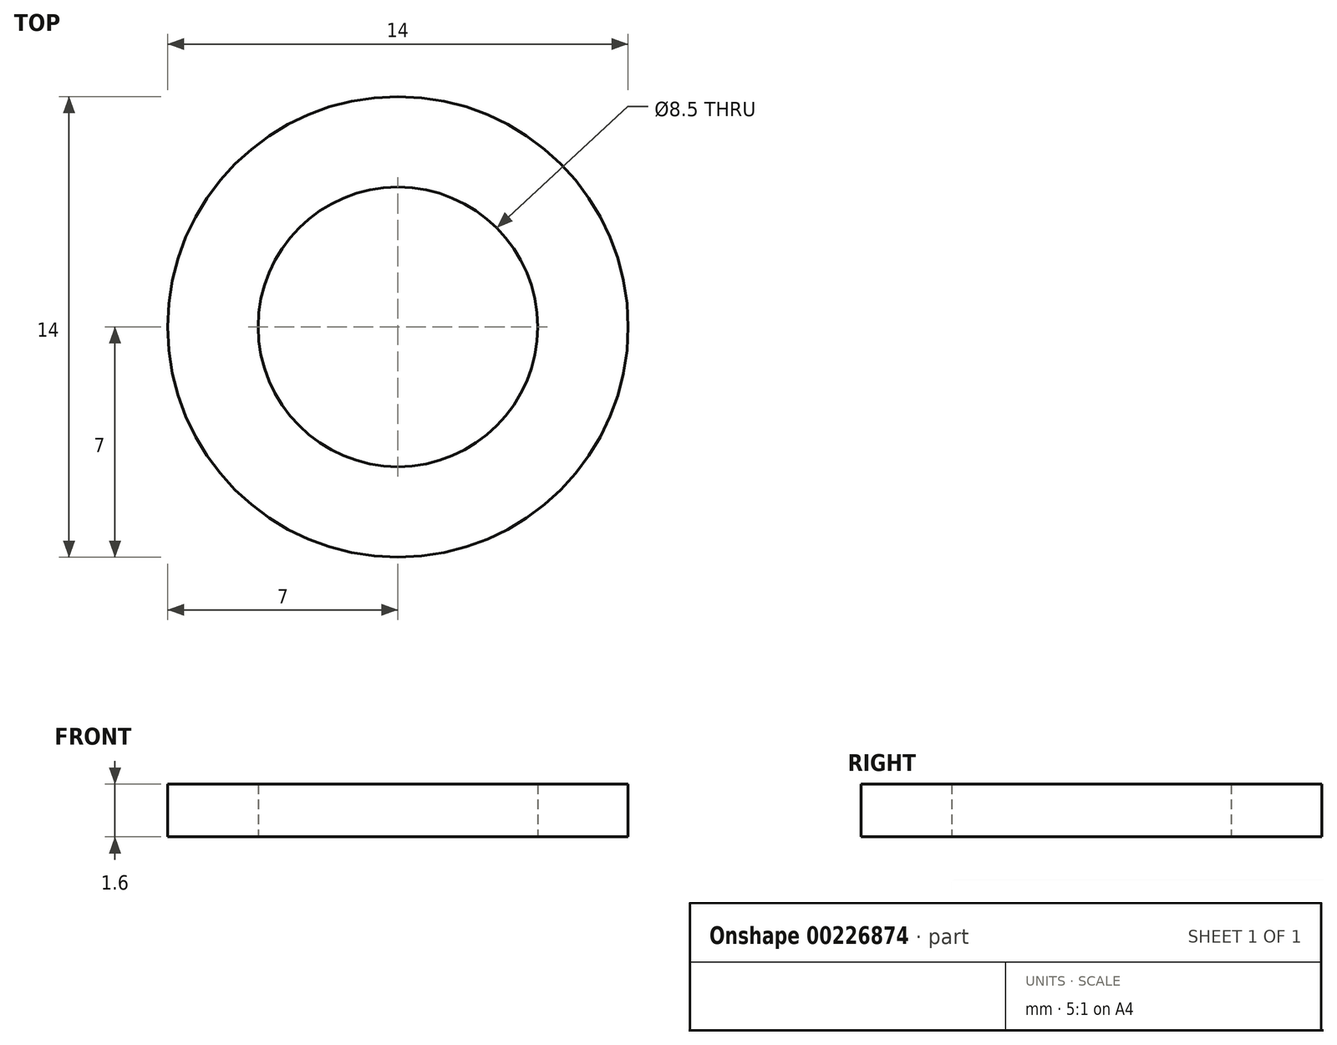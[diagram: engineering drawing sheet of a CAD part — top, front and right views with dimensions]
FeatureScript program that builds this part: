
annotation { "Feature Type Name" : "Feature", "Feature Type Description" : "" }
export const myFeature = defineFeature(function(context is Context, id is Id, definition is map)
    precondition{}
    {
        {
            var Q0;
            Q0=qCreatedBy(makeId("Top.planeOp"),FACE);
            var sketch = newSketch(context, id + "F0", { "sketchPlane" : qUnion([Q0])});
            skCircle(sketch, "E0", {"center": v(0, 0) * mm, "radius": 4.25 * mm});
            skCircle(sketch, "E1", {"center": v(0, 0) * mm, "radius": 7 * mm});
            skSolve(sketch);
        }
        {
            var Q0;
            Q0=makeQuery(id+"F0.imprint","IMPRINT",FACE,{"disambiguationData":[TD([[makeQuery(id+"F0.imprint","IMPRINT",EDGE,{"derivedFrom":sQuery(id+"F0.wireOp",EDGE,"E0")}),-1.0]])]});
            extrude(context, id + "F1", {"entities" : qUnion([Q0]), "depth" : 1.6 * mm});
        }
    });
